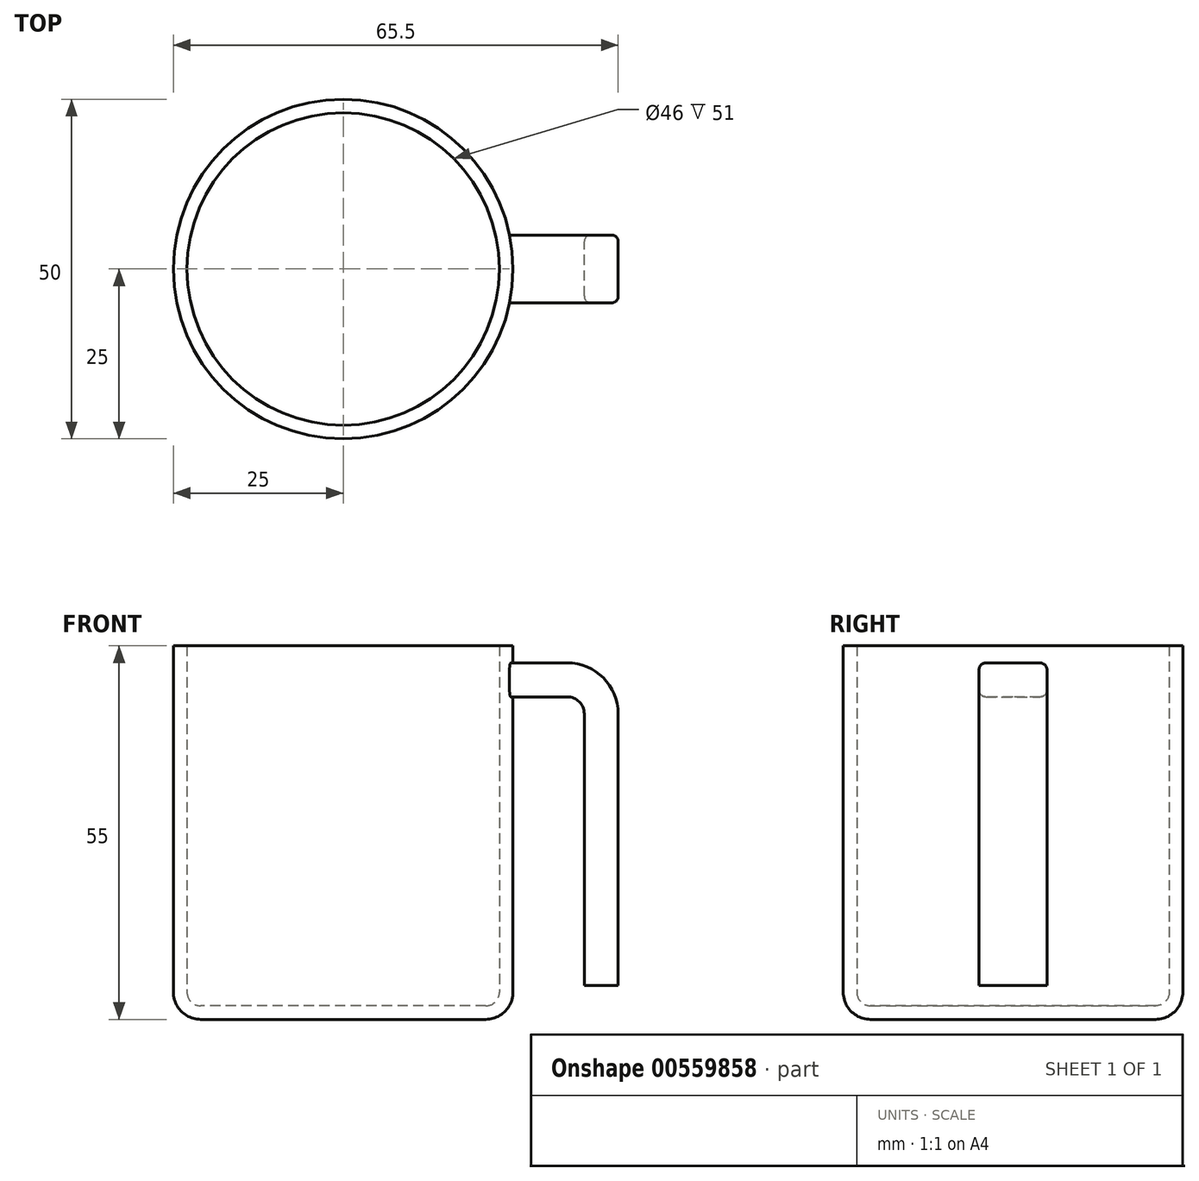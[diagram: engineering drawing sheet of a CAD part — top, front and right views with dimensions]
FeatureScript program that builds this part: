
annotation { "Feature Type Name" : "Feature", "Feature Type Description" : "" }
export const myFeature = defineFeature(function(context is Context, id is Id, definition is map)
    precondition{}
    {
        {
            var Q0;
            Q0=qCreatedBy(makeId("Top.planeOp"),FACE);
            var sketch = newSketch(context, id + "F0", { "sketchPlane" : qUnion([Q0])});
            skCircle(sketch, "E0", {"center": v(0, 0) * mm, "radius": 25 * mm});
            skSolve(sketch);
        }
        {
            var Q0;
            Q0 = qSketchRegion(id + "F0", true);
            extrude(context, id + "F1", {"entities" : qUnion([Q0]), "depth" : 55 * mm, "offsetDistance" : 25 * mm});
        }
        {
            var Q0;
            Q0=makeQuery(id+"F1.opExtrude","CAP_EDGE",EDGE,{"disambiguationData":[OSD([sQuery(id+"F0.wireOp",EDGE,"E0")])],"isStart":true});
            fillet(context, id + "F2", {"entities" : qUnion([Q0]), "radius" : 4 * mm, "tangentPropagation" : true, "allowEdgeOverflow" : false});
        }
        {
            var Q0;
            Q0=makeQuery(id+"F1.opExtrude","CAP_FACE",FACE,{"disambiguationData":[OSD([sQuery(id+"F0.wireOp",EDGE,"E0")])],"isStart":false});
            shell(context, id + "F3", {"entities" : qUnion([Q0]), "thickness" : 2 * mm});
        }
        {
            var Q0;
            Q0=qCreatedBy(makeId("Right.planeOp"),FACE);
            var sketch = newSketch(context, id + "F4", { "sketchPlane" : qUnion([Q0])});
            skLineSegment(sketch, "E1.bottom", {"start": v(-4, 47.5) * mm, "end": v(4, 47.5) * mm});
            skLineSegment(sketch, "E1.top", {"start": v(-4, 52.5) * mm, "end": v(4, 52.5) * mm});
            skLineSegment(sketch, "E1.left", {"start": v(-5, 48.5) * mm, "end": v(-5, 51.5) * mm});
            skLineSegment(sketch, "E1.right", {"start": v(5, 48.5) * mm, "end": v(5, 51.5) * mm});
            skLineSegment(sketch, "E2", {"start": v(-24.1, 50) * mm, "end": v(5, 50) * mm, "construction": true});
            skPoint(sketch, "E2.startSnap0", {"position": v(-5, 50) * mm});
            skPoint(sketch, "E2.endSnap0", {"position": v(5, 50) * mm});
            skLineSegment(sketch, "E3", {"start": v(0, 47.5) * mm, "end": v(0, 52.5) * mm, "construction": true});
            skPoint(sketch, "E4.visualSharp", {"position": v(-5, 52.5) * mm});
            skArc(sketch, "E4.filletArc", {"start": v(-4, 52.5) * mm, "mid": v(-4.7, 52.2) * mm, "end": v(-5, 51.5) * mm});
            skPoint(sketch, "E5.visualSharp", {"position": v(-5, 47.5) * mm});
            skArc(sketch, "E5.filletArc", {"start": v(-5, 48.5) * mm, "mid": v(-4.7, 47.8) * mm, "end": v(-4, 47.5) * mm});
            skPoint(sketch, "E6.visualSharp", {"position": v(5, 47.5) * mm});
            skArc(sketch, "E6.filletArc", {"start": v(4, 47.5) * mm, "mid": v(4.7, 47.8) * mm, "end": v(5, 48.5) * mm});
            skPoint(sketch, "E7.visualSharp", {"position": v(5, 52.5) * mm});
            skArc(sketch, "E7.filletArc", {"start": v(5, 51.5) * mm, "mid": v(4.7, 52.2) * mm, "end": v(4, 52.5) * mm});
            skSolve(sketch);
        }
        {
            var Q0;
            Q0=qCreatedBy(makeId("Front.planeOp"),FACE);
            var sketch = newSketch(context, id + "F5", { "sketchPlane" : qUnion([Q0])});
            skLineSegment(sketch, "E8", {"start": v(0, 50) * mm, "end": v(33, 50) * mm});
            skLineSegment(sketch, "E9", {"start": v(38, 45) * mm, "end": v(38, 5) * mm});
            skPoint(sketch, "E10.visualSharp", {"position": v(38, 50) * mm});
            skArc(sketch, "E10.filletArc", {"start": v(38, 45) * mm, "mid": v(36.54, 48.54) * mm, "end": v(33, 50) * mm});
            skSolve(sketch);
        }
        {
            var Q0;
            Q0 = qSketchRegion(id + "F4", true);
            var Q1;
            Q1 = qConstructionFilter(qBodyType(qCreatedBy(id + "F5" ,EDGE), BodyType.WIRE), ConstructionObject.NO);
            sweep(context, id + "F6", {"operationType" : NewBodyOperationType.ADD, "profiles" : qUnion([Q0]), "path" : qUnion([Q1])});
        }
        {
            var Q0;
            Q0=makeQuery(id+"F6.opSweep","CAP_FACE",FACE,{"disambiguationData":[OSD([sQuery(id+"F4.wireOp",EDGE,"E1.bottom"),sQuery(id+"F4.wireOp",EDGE,"E1.top"),sQuery(id+"F4.wireOp",EDGE,"E1.left"),sQuery(id+"F4.wireOp",EDGE,"E1.right"),sQuery(id+"F5.wireOp",VERTEX,"E8.start")])],"isStart":true});
            var Q1;
            {var subQ0=sQuery(id+"F0.wireOp",EDGE,"E0");Q1=makeQuery(id+"F3.opShell","OFFSET_FACE",FACE,{"disambiguationData":[OSD([subQ0]),TDD([makeQuery(id+"F1.opExtrude","SWEPT_FACE",FACE,{"disambiguationData":[OSD([subQ0])]})])]});}
            extrude(context, id + "F7", {"entities" : qUnion([Q0]), "operationType" : NewBodyOperationType.REMOVE, "endBound" : BoundingType.UP_TO_SURFACE, "oppositeDirection" : true, "depth" : 25 * mm, "endBoundEntityFace" : qUnion([Q1]), "offsetDistance" : 25 * mm});
        }
    });
